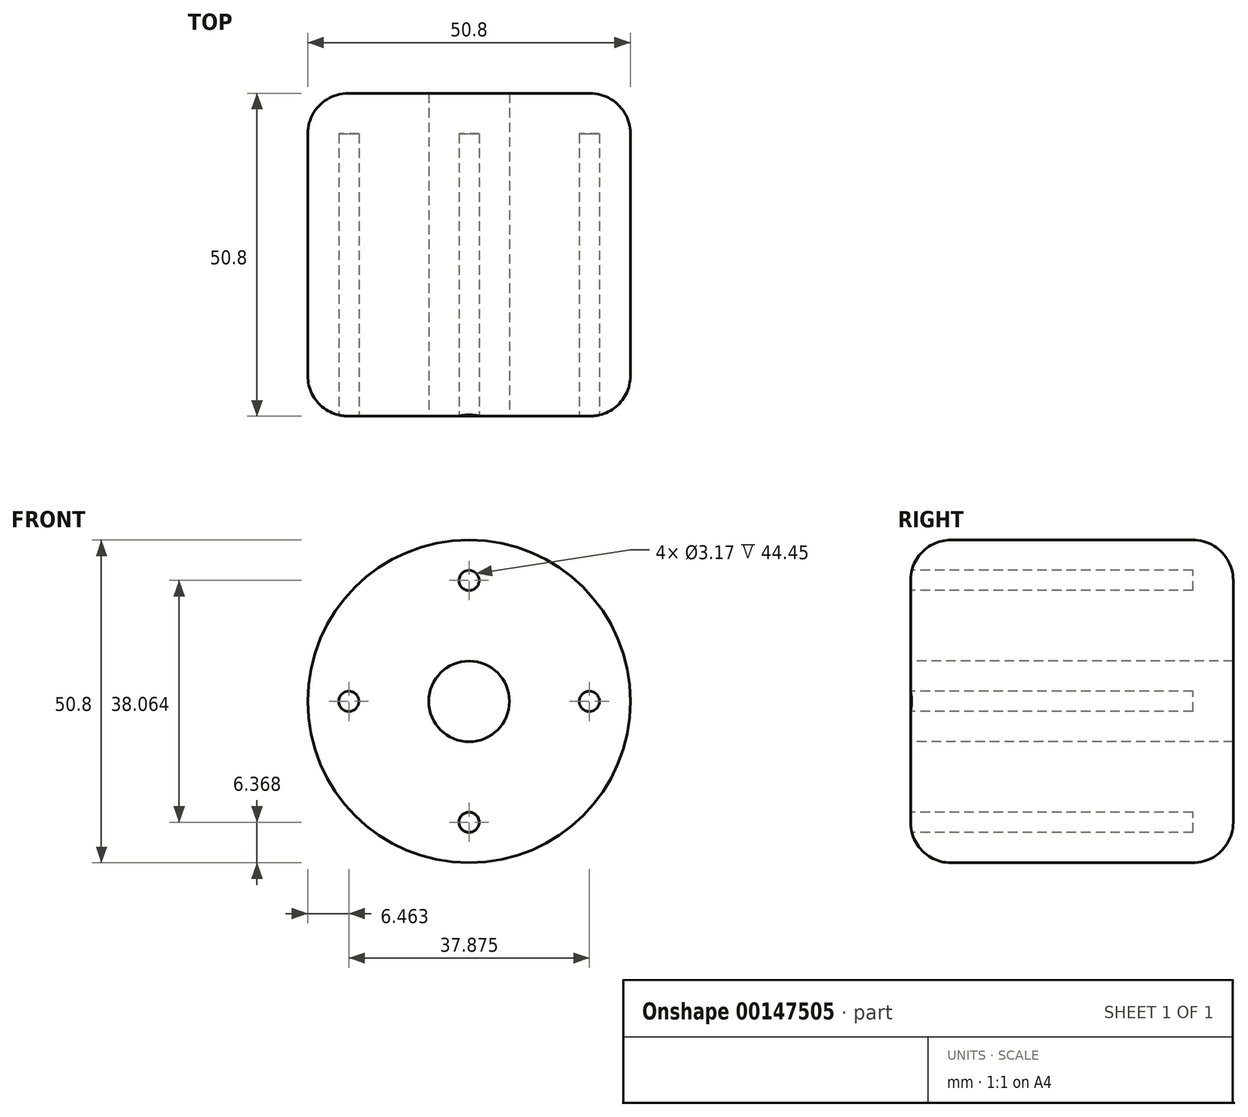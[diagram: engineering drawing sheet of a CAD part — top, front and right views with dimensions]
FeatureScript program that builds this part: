
annotation { "Feature Type Name" : "Feature", "Feature Type Description" : "" }
export const myFeature = defineFeature(function(context is Context, id is Id, definition is map)
    precondition{}
    {
        {
            var Q0;
            Q0=qCreatedBy(makeId("Front.planeOp"),FACE);
            var sketch = newSketch(context, id + "F0", { "sketchPlane" : qUnion([Q0])});
            skCircle(sketch, "E0", {"center": v(0, 0) * mm, "radius": 25.4 * mm});
            skSolve(sketch);
        }
        {
            var Q0;
            Q0 = qSketchRegion(id + "F0", true);
            extrude(context, id + "F1", {"entities" : qUnion([Q0]), "depth" : 50.8 * mm});
        }
        {
            var Q0;
            Q0=makeQuery(id+"F1.opExtrude","CAP_FACE",FACE,{"disambiguationData":[OSD([sQuery(id+"F0.wireOp",EDGE,"E0")])],"isStart":false});
            var sketch = newSketch(context, id + "F2", { "sketchPlane" : qUnion([Q0])});
            skCircle(sketch, "E1", {"center": v(0, 0) * mm, "radius": 6.35 * mm});
            skSolve(sketch);
        }
        {
            var Q0;
            Q0 = qSketchRegion(id + "F2", true);
            extrude(context, id + "F3", {"entities" : qUnion([Q0]), "operationType" : NewBodyOperationType.REMOVE, "oppositeDirection" : true, "depth" : 50.8 * mm});
        }
        {
            var Q0;
            Q0=makeQuery(id+"F1.opExtrude","CAP_FACE",FACE,{"disambiguationData":[OSD([sQuery(id+"F0.wireOp",EDGE,"E0")])],"isStart":false});
            var sketch = newSketch(context, id + "F4", { "sketchPlane" : qUnion([Q0])});
            skCircle(sketch, "E2", {"center": v(0, 19.03) * mm, "radius": 1.59 * mm});
            skCircle(sketch, "E3", {"center": v(18.94, 0) * mm, "radius": 1.59 * mm});
            skCircle(sketch, "E4", {"center": v(0, -19.03) * mm, "radius": 1.59 * mm});
            skCircle(sketch, "E5", {"center": v(-18.94, 0) * mm, "radius": 1.59 * mm});
            skPoint(sketch, "E6.center.orphan", {"position": v(0, 0) * mm});
            skSolve(sketch);
        }
        {
            var Q0;
            Q0 = qSketchRegion(id + "F4", true);
            extrude(context, id + "F5", {"entities" : qUnion([Q0]), "operationType" : NewBodyOperationType.REMOVE, "oppositeDirection" : true, "depth" : 44.45 * mm});
        }
        {
            var Q0;
            Q0=makeQuery(id+"F1.opExtrude","CAP_EDGE",EDGE,{"disambiguationData":[OSD([sQuery(id+"F0.wireOp",EDGE,"E0")])],"isStart":false});
            fillet(context, id + "F6", {"entities" : qUnion([Q0]), "radius" : 6.35 * mm, "tangentPropagation" : true, "allowEdgeOverflow" : false});
        }
        {
            var Q0;
            Q0=makeQuery(id+"F1.opExtrude","CAP_EDGE",EDGE,{"disambiguationData":[OSD([sQuery(id+"F0.wireOp",EDGE,"E0")])],"isStart":true});
            fillet(context, id + "F7", {"entities" : qUnion([Q0]), "radius" : 6.35 * mm, "tangentPropagation" : true, "allowEdgeOverflow" : false});
        }
    });
